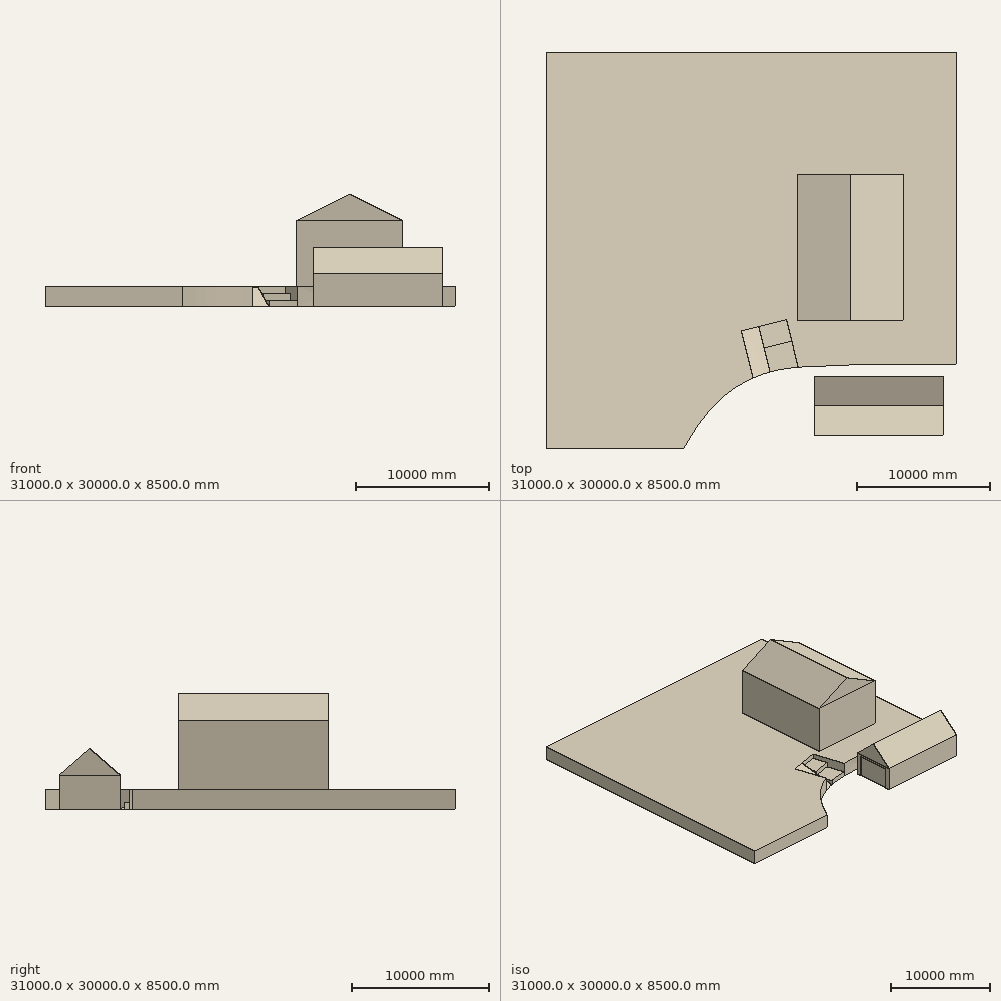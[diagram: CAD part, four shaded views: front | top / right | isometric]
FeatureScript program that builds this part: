
annotation { "Feature Type Name" : "Feature", "Feature Type Description" : "" }
export const myFeature = defineFeature(function(context is Context, id is Id, definition is map)
    precondition{}
    {
        {
            var Q0;
            Q0=qCreatedBy(makeId("Top.planeOp"),FACE);
            var sketch = newSketch(context, id + "F0", { "sketchPlane" : qUnion([Q0])});
            skLineSegment(sketch, "E0.bottom", {"start": v(15378.63, -9863.8) * mm, "end": v(-15621.37, -9863.8) * mm});
            skLineSegment(sketch, "E0.top", {"start": v(15378.63, 20136.2) * mm, "end": v(-15621.37, 20136.2) * mm});
            skLineSegment(sketch, "E0.left", {"start": v(15378.63, -9863.8) * mm, "end": v(15378.63, 20136.2) * mm});
            skLineSegment(sketch, "E0.right", {"start": v(-15621.37, -9863.8) * mm, "end": v(-15621.37, 20136.2) * mm});
            skPoint(sketch, "E1", {"position": v(14378.63, -8863.8) * mm});
            skLineSegment(sketch, "E2.bottom", {"start": v(14378.63, -8863.8) * mm, "end": v(4678.63, -8863.8) * mm});
            skLineSegment(sketch, "E2.top", {"start": v(14378.63, -4363.8) * mm, "end": v(4678.63, -4363.8) * mm});
            skLineSegment(sketch, "E2.left", {"start": v(14378.63, -8863.8) * mm, "end": v(14378.63, -4363.8) * mm});
            skLineSegment(sketch, "E2.right", {"start": v(4678.63, -8863.8) * mm, "end": v(4678.63, -4363.8) * mm});
            skFitSpline(sketch, "E3", {"points": [v(-5256.01, -9863.8) * mm, v(0, -4532.45) * mm, v(15378.63, -3490.14) * mm], "startDerivative": vector(14599.33, 26044.06) * mm, "endDerivative": vector(59112.39, -261.37) * mm});
            skLineSegment(sketch, "E4", {"start": v(0, -4532.45) * mm, "end": v(3414.26, -3687) * mm});
            skLineSegment(sketch, "E5", {"start": v(3414.26, -3687) * mm, "end": v(2927.4, -1720.88) * mm});
            skLineSegment(sketch, "E6", {"start": v(-486.86, -2566.33) * mm, "end": v(0, -4532.45) * mm});
            skLineSegment(sketch, "E7", {"start": v(-486.86, -2566.33) * mm, "end": v(-888.53, -944.22) * mm});
            skLineSegment(sketch, "E8", {"start": v(2525.73, -98.77) * mm, "end": v(2927.4, -1720.88) * mm});
            skLineSegment(sketch, "E9", {"start": v(432.1, -617.2) * mm, "end": v(833.78, -2239.31) * mm});
            skLineSegment(sketch, "E10", {"start": v(833.78, -2239.31) * mm, "end": v(1320.63, -4205.43) * mm});
            skLineSegment(sketch, "E11", {"start": v(-888.53, -944.22) * mm, "end": v(432.1, -617.2) * mm});
            skLineSegment(sketch, "E12", {"start": v(2525.73, -98.77) * mm, "end": v(432.1, -617.2) * mm});
            skLineSegment(sketch, "E13", {"start": v(2927.4, -1720.88) * mm, "end": v(833.78, -2239.31) * mm});
            skSolve(sketch);
        }
        {
            var Q0;
            Q0=makeQuery(id+"F0.imprint","IMPRINT",FACE,{"disambiguationData":[TD([[makeQuery(id+"F0.imprint","IMPRINT",EDGE,{"derivedFrom":sQuery(id+"F0.wireOp",EDGE,"E2.bottom")}),-1.0]])]});
            extrude(context, id + "F1", {"entities" : qUnion([Q0]), "depth" : 2500 * mm, "offsetDistance" : 25 * mm});
        }
        {
            var Q0;
            Q0=makeQuery(id+"F1.opExtrude","CAP_FACE",FACE,{"disambiguationData":[OSD([sQuery(id+"F0.wireOp",EDGE,"E2.bottom"),sQuery(id+"F0.wireOp",EDGE,"E2.top"),sQuery(id+"F0.wireOp",EDGE,"E2.left"),sQuery(id+"F0.wireOp",EDGE,"E2.right")])],"isStart":false});
            extrude(context, id + "F2", {"entities" : qUnion([Q0]), "depth" : 2000 * mm, "offsetDistance" : 25 * mm});
        }
        {
            var Q0;
            Q0=makeQuery(id+"F2.opExtrude","CAP_EDGE",EDGE,{"disambiguationData":[OSD([sQuery(id+"F0.wireOp",EDGE,"E2.bottom")])],"isStart":false});
            var Q1;
            Q1=makeQuery(id+"F2.opExtrude","CAP_EDGE",EDGE,{"disambiguationData":[OSD([sQuery(id+"F0.wireOp",EDGE,"E2.top")])],"isStart":false});
            chamfer(context, id + "F3", {"entities" : qUnion([Q0, Q1]), "chamferType" : ChamferType.TWO_OFFSETS, "width1" : 2000 * mm, "oppositeDirection" : false, "width2" : 2300 * mm, "tangentPropagation" : true});
        }
        {
            var Q0;
            Q0=makeQuery(id+"F1.opExtrude","SWEPT_FACE",FACE,{"disambiguationData":[OSD([sQuery(id+"F0.wireOp",EDGE,"E2.right")])]});
            var sketch = newSketch(context, id + "F4", { "sketchPlane" : qUnion([Q0])});
            skLineSegment(sketch, "E14.bottom", {"start": v(8412.18, 2210.86) * mm, "end": v(4738.5, 2210.86) * mm});
            skLineSegment(sketch, "E14.top", {"start": v(8412.18, 0) * mm, "end": v(4738.5, 0) * mm});
            skLineSegment(sketch, "E14.left", {"start": v(8412.18, 2210.86) * mm, "end": v(8412.18, 0) * mm});
            skLineSegment(sketch, "E14.right", {"start": v(4738.5, 2210.86) * mm, "end": v(4738.5, 0) * mm});
            skSolve(sketch);
        }
        {
            var Q0;
            Q0=makeQuery(id+"F4.imprint","IMPRINT",FACE,{"disambiguationData":[TD([[makeQuery(id+"F4.imprint","IMPRINT",EDGE,{"derivedFrom":sQuery(id+"F4.wireOp",EDGE,"E14.bottom")}),1.0]])]});
            extrude(context, id + "F5", {"entities" : qUnion([Q0]), "operationType" : NewBodyOperationType.REMOVE, "oppositeDirection" : true, "depth" : 100 * mm, "offsetDistance" : 25 * mm});
        }
        {
            var Q0;
            {var subQ2=sQuery(id+"F0.wireOp",EDGE,"E0.top");Q0=makeQuery(id+"F0.imprint","IMPRINT",FACE,{"disambiguationData":[TD([[makeQuery(id+"F0.imprint","IMPRINT",EDGE,{"derivedFrom":subQ2}),1.0]])]});}
            extrude(context, id + "F6", {"entities" : qUnion([Q0]), "depth" : 1500 * mm, "offsetDistance" : 25 * mm});
        }
        {
            var Q0;
            Q0=makeQuery(id+"F6.opExtrude","CAP_FACE",FACE,{"disambiguationData":[OSD([sQuery(id+"F0.wireOp",EDGE,"E0.bottom"),sQuery(id+"F0.wireOp",EDGE,"E0.top"),sQuery(id+"F0.wireOp",EDGE,"E0.left"),sQuery(id+"F0.wireOp",EDGE,"E0.right"),sQuery(id+"F0.wireOp",EDGE,"E3"),sQuery(id+"F0.wireOp",EDGE,"E5"),sQuery(id+"F0.wireOp",EDGE,"E6"),sQuery(id+"F0.wireOp",EDGE,"E7"),sQuery(id+"F0.wireOp",EDGE,"GhdPftz5-I5fB-ies3-EDJ3-55ahAig9F6fH"),sQuery(id+"F0.wireOp",EDGE,"E8")])],"isStart":false});
            var sketch = newSketch(context, id + "F7", { "sketchPlane" : qUnion([Q0])});
            skLineSegment(sketch, "E15.bottom", {"start": v(3378.63, -139.07) * mm, "end": v(11378.63, -139.07) * mm});
            skLineSegment(sketch, "E15.top", {"start": v(3378.63, 10860.93) * mm, "end": v(11378.63, 10860.93) * mm});
            skLineSegment(sketch, "E15.left", {"start": v(3378.63, -139.07) * mm, "end": v(3378.63, 10860.93) * mm});
            skLineSegment(sketch, "E15.right", {"start": v(11378.63, -139.07) * mm, "end": v(11378.63, 10860.93) * mm});
            skSolve(sketch);
        }
        {
            var Q0;
            Q0=makeQuery(id+"F7.imprint","IMPRINT",FACE,{"disambiguationData":[TD([[makeQuery(id+"F7.imprint","IMPRINT",EDGE,{"derivedFrom":sQuery(id+"F7.wireOp",EDGE,"E15.bottom")}),1.0]])]});
            extrude(context, id + "F8", {"entities" : qUnion([Q0]), "depth" : 5000 * mm, "offsetDistance" : 25 * mm});
        }
        {
            var Q0;
            Q0=makeQuery(id+"F8.opExtrude","CAP_FACE",FACE,{"disambiguationData":[OSD([sQuery(id+"F7.wireOp",EDGE,"E15.bottom"),sQuery(id+"F7.wireOp",EDGE,"E15.top"),sQuery(id+"F7.wireOp",EDGE,"E15.left"),sQuery(id+"F7.wireOp",EDGE,"E15.right")])],"isStart":false});
            extrude(context, id + "F9", {"entities" : qUnion([Q0]), "depth" : 2000 * mm, "offsetDistance" : 25 * mm});
        }
        {
            var Q0;
            Q0=makeQuery(id+"F9.opExtrude","CAP_EDGE",EDGE,{"disambiguationData":[OSD([sQuery(id+"F7.wireOp",EDGE,"E15.left")])],"isStart":false});
            var Q1;
            Q1=makeQuery(id+"F9.opExtrude","CAP_EDGE",EDGE,{"disambiguationData":[OSD([sQuery(id+"F7.wireOp",EDGE,"E15.right")])],"isStart":false});
            chamfer(context, id + "F10", {"entities" : qUnion([Q0, Q1]), "chamferType" : ChamferType.TWO_OFFSETS, "width1" : 2000 * mm, "oppositeDirection" : false, "width2" : 4000 * mm, "tangentPropagation" : true});
        }
        {
            var Q0;
            {var subQ0=sQuery(id+"F0.wireOp",EDGE,"E5");Q0=makeQuery(id+"F0.imprint","IMPRINT",FACE,{"disambiguationData":[TD([[makeQuery(id+"F0.imprint","IMPRINT",EDGE,{"derivedFrom":subQ0}),1.0]])]});}
            extrude(context, id + "F11", {"entities" : qUnion([Q0]), "depth" : 500 * mm, "offsetDistance" : 25 * mm});
        }
        {
            var Q0;
            Q0=makeQuery(id+"F0.imprint","IMPRINT",FACE,{"disambiguationData":[TD([[makeQuery(id+"F0.imprint","IMPRINT",EDGE,{"derivedFrom":sQuery(id+"F0.wireOp",EDGE,"E8")}),-1.0]])]});
            extrude(context, id + "F12", {"entities" : qUnion([Q0]), "depth" : 1000 * mm, "offsetDistance" : 25 * mm});
        }
        {
            var Q0;
            {var subQ1=sQuery(id+"F0.wireOp",EDGE,"E6");Q0=makeQuery(id+"F0.imprint","IMPRINT",FACE,{"disambiguationData":[TD([[makeQuery(id+"F0.imprint","IMPRINT",EDGE,{"derivedFrom":subQ1}),1.0]])]});}
            extrude(context, id + "F13", {"entities" : qUnion([Q0]), "depth" : 1500 * mm, "offsetDistance" : 25 * mm});
        }
        {
            var Q0;
            Q0=makeQuery(id+"F13.opExtrude","CAP_EDGE",EDGE,{"disambiguationData":[OSD([sQuery(id+"F0.wireOp",EDGE,"E3")])],"isStart":false});
            chamfer(context, id + "F14", {"entities" : qUnion([Q0]), "chamferType" : ChamferType.TWO_OFFSETS, "width1" : 3600 * mm, "oppositeDirection" : false, "width2" : 1500 * mm, "tangentPropagation" : true});
        }
    });
